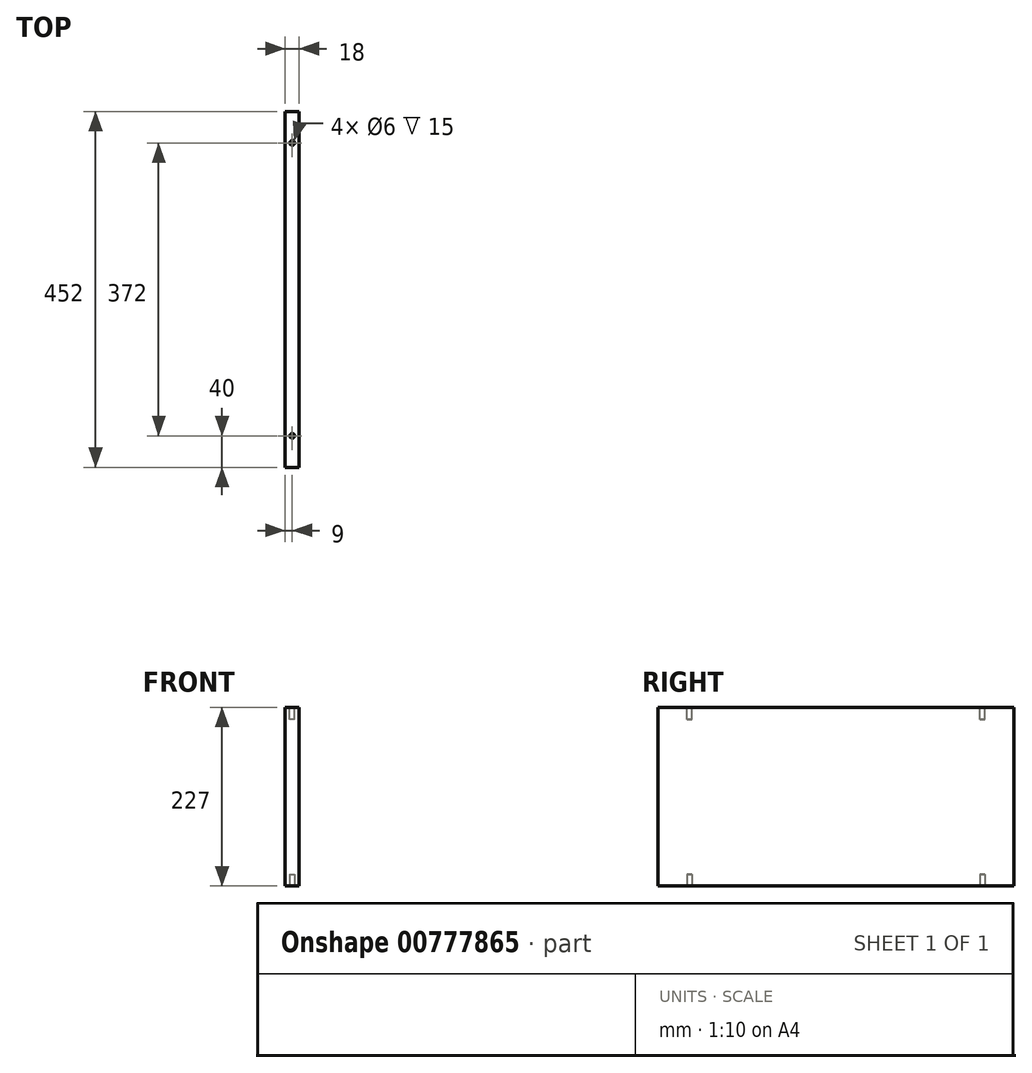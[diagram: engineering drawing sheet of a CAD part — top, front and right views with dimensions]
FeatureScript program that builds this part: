
annotation { "Feature Type Name" : "Feature", "Feature Type Description" : "" }
export const myFeature = defineFeature(function(context is Context, id is Id, definition is map)
    precondition{}
    {
        {
            var Q0;
            Q0=qCreatedBy(makeId("Right.planeOp"),FACE);
            var sketch = newSketch(context, id + "F0", { "sketchPlane" : qUnion([Q0])});
            skLineSegment(sketch, "E0.bottom", {"start": v(-226, 113.5) * mm, "end": v(226, 113.5) * mm});
            skLineSegment(sketch, "E0.top", {"start": v(-226, -113.5) * mm, "end": v(226, -113.5) * mm});
            skLineSegment(sketch, "E0.left", {"start": v(-226, 113.5) * mm, "end": v(-226, -113.5) * mm});
            skLineSegment(sketch, "E0.right", {"start": v(226, 113.5) * mm, "end": v(226, -113.5) * mm});
            skSolve(sketch);
        }
        {
            var Q0;
            Q0 = qSketchRegion(id + "F0", true);
            extrude(context, id + "F1", {"entities" : qUnion([Q0]), "endBound" : BoundingType.SYMMETRIC, "depth" : 18 * mm, "offsetDistance" : 25 * mm});
        }
        {
            var Q0;
            Q0=makeQuery(id+"F1.opExtrude","SWEPT_FACE",FACE,{"disambiguationData":[OSD([sQuery(id+"F0.wireOp",EDGE,"E0.bottom")])]});
            var sketch = newSketch(context, id + "F2", { "sketchPlane" : qUnion([Q0])});
            skCircle(sketch, "E1", {"center": v(0, -186) * mm, "radius": 3 * mm});
            skCircle(sketch, "E2", {"center": v(0, 186) * mm, "radius": 3 * mm});
            skSolve(sketch);
        }
        {
            var Q0;
            Q0 = qSketchRegion(id + "F2", true);
            extrude(context, id + "F3", {"entities" : qUnion([Q0]), "operationType" : NewBodyOperationType.REMOVE, "oppositeDirection" : true, "depth" : 15 * mm, "offsetDistance" : 25 * mm});
        }
        {
            var Q0;
            Q0=makeQuery(id+"F1.opExtrude","SWEPT_FACE",FACE,{"disambiguationData":[OSD([sQuery(id+"F0.wireOp",EDGE,"E0.top")])]});
            var sketch = newSketch(context, id + "F4", { "sketchPlane" : qUnion([Q0])});
            skCircle(sketch, "E3", {"center": v(0, 186) * mm, "radius": 3 * mm});
            skCircle(sketch, "E4", {"center": v(0, -186) * mm, "radius": 3 * mm});
            skSolve(sketch);
        }
        {
            var Q0;
            Q0 = qSketchRegion(id + "F4", true);
            extrude(context, id + "F5", {"entities" : qUnion([Q0]), "operationType" : NewBodyOperationType.REMOVE, "oppositeDirection" : true, "depth" : 15 * mm, "offsetDistance" : 25 * mm});
        }
    });
